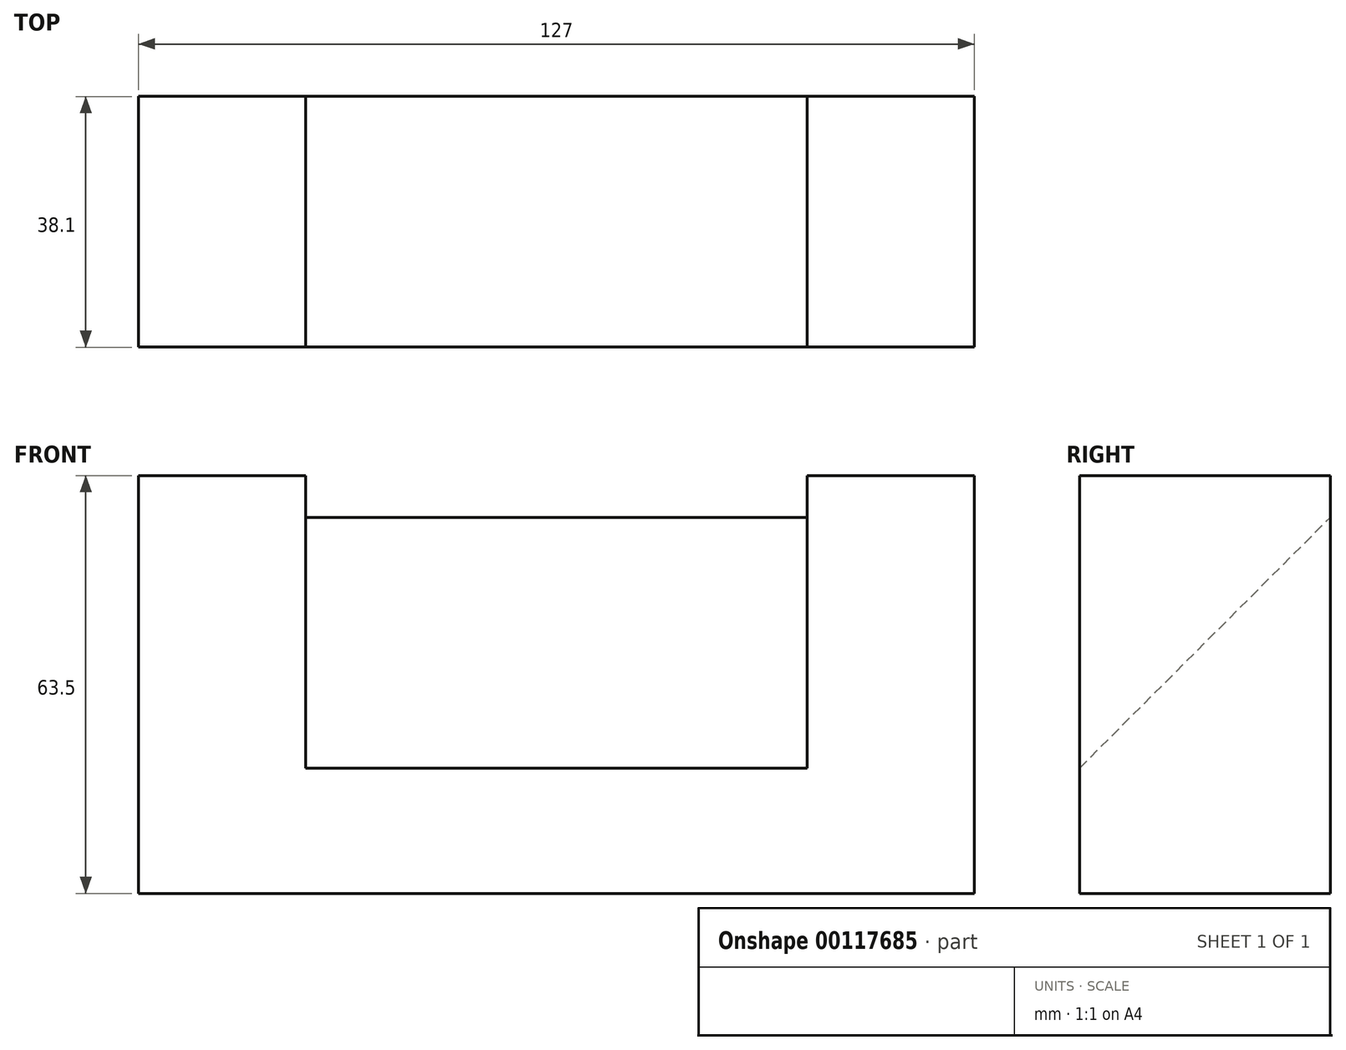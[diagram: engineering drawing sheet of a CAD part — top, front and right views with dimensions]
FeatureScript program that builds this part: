
annotation { "Feature Type Name" : "Feature", "Feature Type Description" : "" }
export const myFeature = defineFeature(function(context is Context, id is Id, definition is map)
    precondition{}
    {
        {
            var Q0;
            Q0=qCreatedBy(makeId("Right.planeOp"),FACE);
            var sketch = newSketch(context, id + "F0", { "sketchPlane" : qUnion([Q0])});
            skLineSegment(sketch, "E0.bottom", {"start": v(-0.79, 32.06) * mm, "end": v(37.31, 32.06) * mm});
            skLineSegment(sketch, "E0.top", {"start": v(-0.79, -31.44) * mm, "end": v(37.31, -31.44) * mm});
            skLineSegment(sketch, "E0.left", {"start": v(-0.79, 32.06) * mm, "end": v(-0.79, -31.44) * mm});
            skLineSegment(sketch, "E0.right", {"start": v(37.31, 32.06) * mm, "end": v(37.31, -31.44) * mm});
            skSolve(sketch);
        }
        {
            var Q0;
            Q0 = qSketchRegion(id + "F0", true);
            extrude(context, id + "F1", {"entities" : qUnion([Q0]), "depth" : 76.2 * mm});
        }
        {
            var Q0;
            Q0=makeQuery(id+"F1.opExtrude","CAP_FACE",FACE,{"disambiguationData":[OSD([sQuery(id+"F0.wireOp",EDGE,"E0.bottom"),sQuery(id+"F0.wireOp",EDGE,"E0.top"),sQuery(id+"F0.wireOp",EDGE,"E0.left"),sQuery(id+"F0.wireOp",EDGE,"E0.right")])],"isStart":false});
            var sketch = newSketch(context, id + "F2", { "sketchPlane" : qUnion([Q0])});
            skLineSegment(sketch, "E1", {"start": v(-0.79, -12.39) * mm, "end": v(37.31, 25.71) * mm});
            skPoint(sketch, "E2.end.orphan", {"position": v(-0.79, 25.71) * mm});
            skLineSegment(sketch, "E3", {"start": v(37.31, 25.71) * mm, "end": v(37.31, 32.06) * mm});
            skLineSegment(sketch, "E4", {"start": v(37.31, 32.06) * mm, "end": v(-0.79, 32.06) * mm});
            skLineSegment(sketch, "E5", {"start": v(-0.79, 32.06) * mm, "end": v(-0.79, -12.39) * mm});
            skSolve(sketch);
        }
        {
            var Q0;
            Q0 = qSketchRegion(id + "F2", true);
            extrude(context, id + "F3", {"entities" : qUnion([Q0]), "operationType" : NewBodyOperationType.REMOVE, "oppositeDirection" : true, "depth" : 76.2 * mm});
        }
        {
            var Q0;
            Q0=makeQuery(id+"F1.opExtrude","CAP_FACE",FACE,{"disambiguationData":[OSD([sQuery(id+"F0.wireOp",EDGE,"E0.bottom"),sQuery(id+"F0.wireOp",EDGE,"E0.top"),sQuery(id+"F0.wireOp",EDGE,"E0.left"),sQuery(id+"F0.wireOp",EDGE,"E0.right")])],"isStart":false});
            var sketch = newSketch(context, id + "F4", { "sketchPlane" : qUnion([Q0])});
            skLineSegment(sketch, "E6.bottom", {"start": v(-0.79, -31.44) * mm, "end": v(37.31, -31.44) * mm});
            skLineSegment(sketch, "E6.top", {"start": v(-0.79, 32.06) * mm, "end": v(37.31, 32.06) * mm});
            skLineSegment(sketch, "E6.left", {"start": v(-0.79, -31.44) * mm, "end": v(-0.79, 32.06) * mm});
            skLineSegment(sketch, "E6.right", {"start": v(37.31, -31.44) * mm, "end": v(37.31, 32.06) * mm});
            skSolve(sketch);
        }
        {
            var Q0;
            Q0 = qSketchRegion(id + "F4", true);
            extrude(context, id + "F5", {"entities" : qUnion([Q0]), "operationType" : NewBodyOperationType.ADD, "depth" : 25.4 * mm});
        }
        {
            var Q0;
            Q0=makeQuery(id+"F1.opExtrude","CAP_FACE",FACE,{"disambiguationData":[OSD([sQuery(id+"F0.wireOp",EDGE,"E0.bottom"),sQuery(id+"F0.wireOp",EDGE,"E0.top"),sQuery(id+"F0.wireOp",EDGE,"E0.left"),sQuery(id+"F0.wireOp",EDGE,"E0.right")])],"isStart":true});
            var sketch = newSketch(context, id + "F6", { "sketchPlane" : qUnion([Q0])});
            skLineSegment(sketch, "E7.bottom", {"start": v(0.79, -31.44) * mm, "end": v(-37.31, -31.44) * mm});
            skLineSegment(sketch, "E7.top", {"start": v(0.79, 32.06) * mm, "end": v(-37.31, 32.06) * mm});
            skLineSegment(sketch, "E7.left", {"start": v(0.79, -31.44) * mm, "end": v(0.79, 32.06) * mm});
            skLineSegment(sketch, "E7.right", {"start": v(-37.31, -31.44) * mm, "end": v(-37.31, 32.06) * mm});
            skSolve(sketch);
        }
        {
            var Q0;
            Q0 = qSketchRegion(id + "F6", true);
            extrude(context, id + "F7", {"entities" : qUnion([Q0]), "operationType" : NewBodyOperationType.ADD, "depth" : 25.4 * mm});
        }
    });
